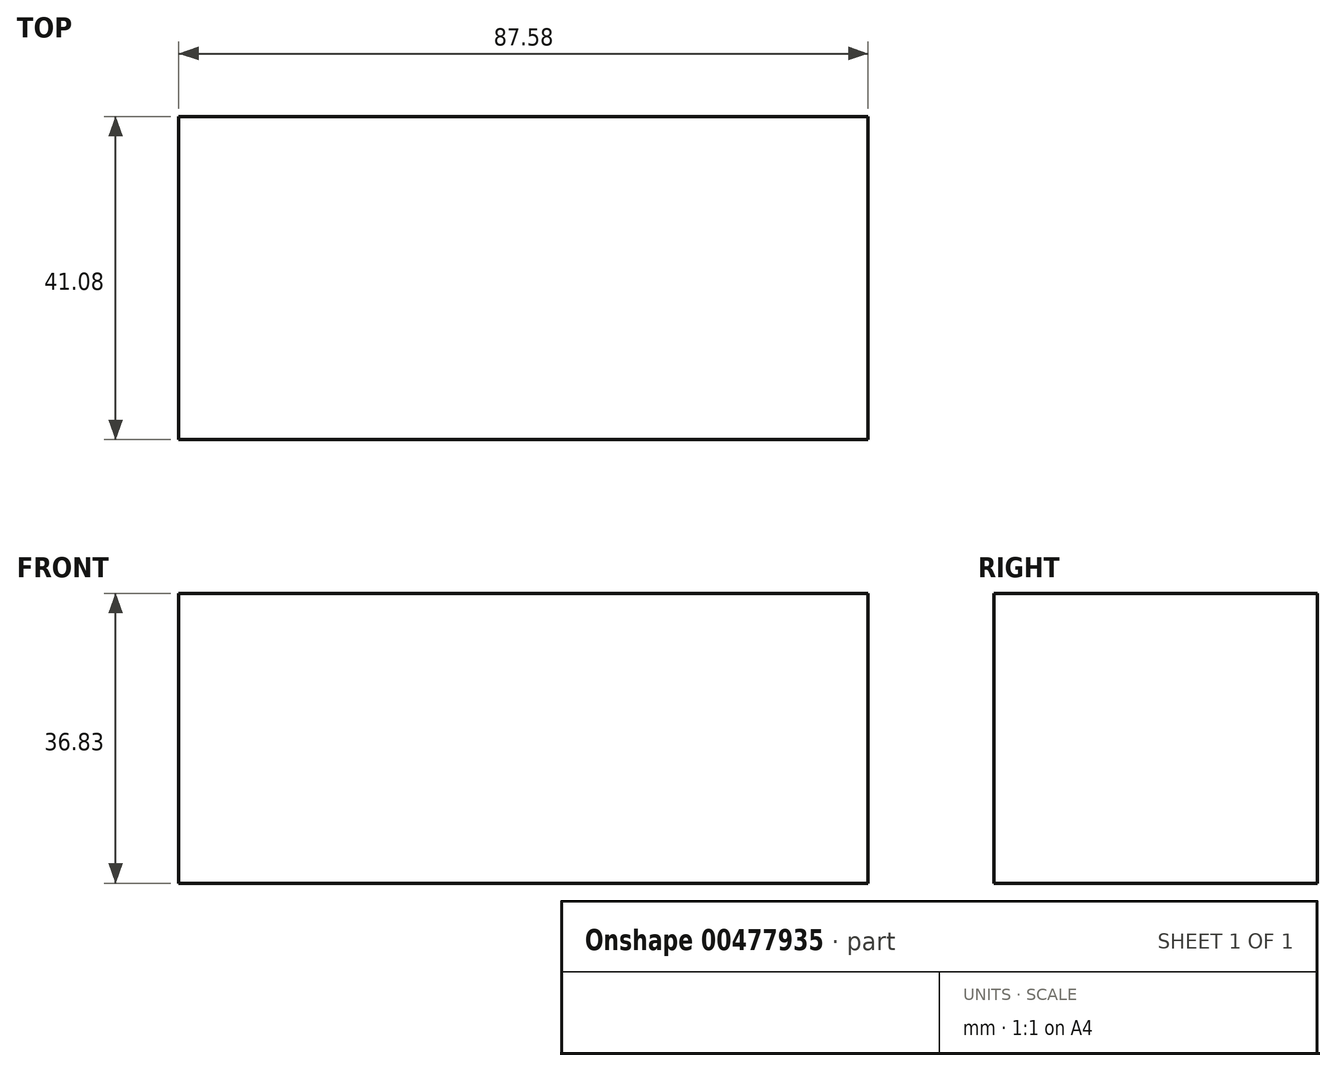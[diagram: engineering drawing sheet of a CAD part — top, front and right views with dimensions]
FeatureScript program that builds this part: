
annotation { "Feature Type Name" : "Feature", "Feature Type Description" : "" }
export const myFeature = defineFeature(function(context is Context, id is Id, definition is map)
    precondition{}
    {
        {
            var Q0;
            Q0=qCreatedBy(makeId("Top.planeOp"),FACE);
            var sketch = newSketch(context, id + "F0", { "sketchPlane" : qUnion([Q0])});
            skLineSegment(sketch, "E0.bottom", {"start": v(0, 0) * mm, "end": v(87.58, 0) * mm});
            skLineSegment(sketch, "E0.top", {"start": v(0, 41.08) * mm, "end": v(87.58, 41.08) * mm});
            skLineSegment(sketch, "E0.left", {"start": v(0, 0) * mm, "end": v(0, 41.08) * mm});
            skLineSegment(sketch, "E0.right", {"start": v(87.58, 0) * mm, "end": v(87.58, 41.08) * mm});
            skSolve(sketch);
        }
        {
            var Q0;
            Q0=makeQuery(id+"F0.imprint","IMPRINT",FACE,{"disambiguationData":[TD([[makeQuery(id+"F0.imprint","IMPRINT",EDGE,{"derivedFrom":sQuery(id+"F0.wireOp",EDGE,"E0.bottom")}),1.0]])]});
            extrude(context, id + "F1", {"entities" : qUnion([Q0]), "depth" : 36.83 * mm});
        }
    });
